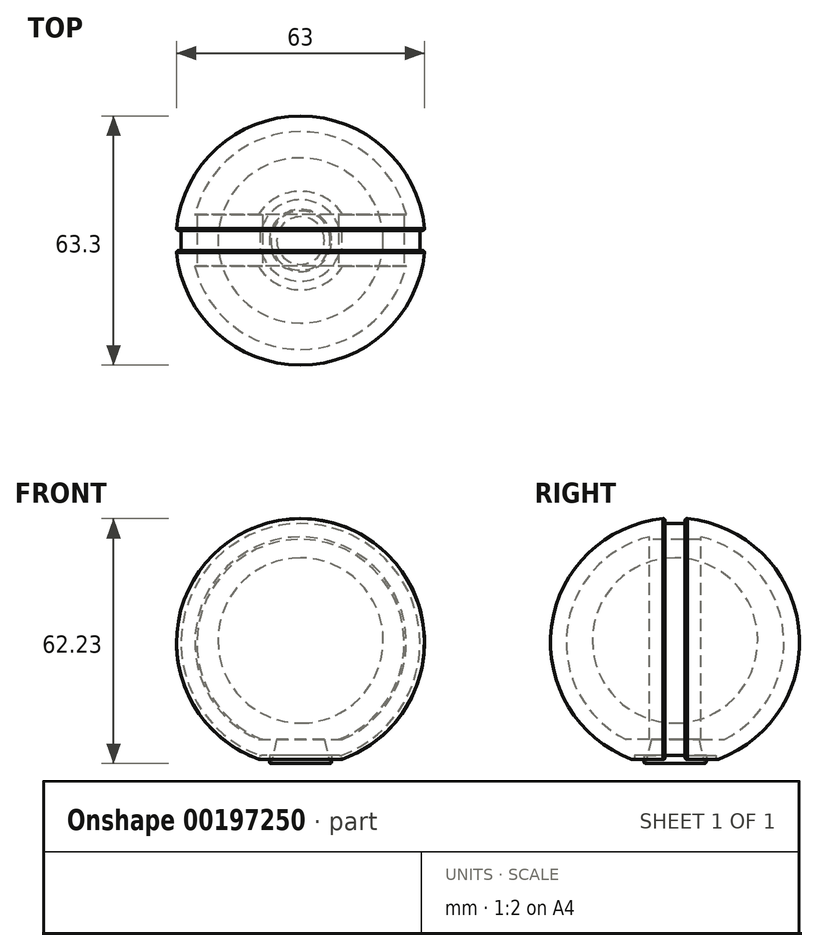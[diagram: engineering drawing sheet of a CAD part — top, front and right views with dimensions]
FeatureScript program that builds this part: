
annotation { "Feature Type Name" : "Feature", "Feature Type Description" : "" }
export const myFeature = defineFeature(function(context is Context, id is Id, definition is map)
    precondition{}
    {
        {
            var Q0;
            Q0=qCreatedBy(makeId("Front.planeOp"),FACE);
            var sketch = newSketch(context, id + "F0", { "sketchPlane" : qUnion([Q0])});
            skLineSegment(sketch, "E0", {"start": v(0, 0) * mm, "end": v(0, 63.3) * mm});
            skArc(sketch, "E1", {"start": v(0, 63.3) * mm, "mid": v(-31.65, 31.65) * mm, "end": v(0, 0) * mm});
            skSolve(sketch);
        }
        {
            var Q0;
            Q0 = qSketchRegion(id + "F0", true);
            var Q1;
            Q1=sQuery(id+"F0.wireOp",EDGE,"E0");
            revolve(context, id + "F1", {"entities" : qUnion([Q0]), "axis" : qUnion([Q1]), "revolveType" : RevolveType.FULL});
        }
        {
            var Q0;
            Q0=qCreatedBy(makeId("Front.planeOp"),FACE);
            var sketch = newSketch(context, id + "F2", { "sketchPlane" : qUnion([Q0])});
            skLineSegment(sketch, "E2", {"start": v(10, -3.8) * mm, "end": v(10, 2.88) * mm});
            skLineSegment(sketch, "E3", {"start": v(-10, 2.88) * mm, "end": v(-10, -3.8) * mm});
            skLineSegment(sketch, "E4", {"start": v(0, 0) * mm, "end": v(0, 63.04) * mm, "construction": true});
            skArc(sketch, "E5", {"start": v(10, 2.88) * mm, "mid": v(0, 61.85) * mm, "end": v(-10, 2.88) * mm});
            skArc(sketch, "E6", {"start": v(10, -3.8) * mm, "mid": v(0, 68.23) * mm, "end": v(-10, -3.8) * mm});
            skSolve(sketch);
        }
        {
            var Q0;
            Q0 = qSketchRegion(id + "F2", true);
            extrude(context, id + "F3", {"entities" : qUnion([Q0]), "operationType" : NewBodyOperationType.REMOVE, "oppositeDirection" : true, "depth" : 2.54 * mm, "hasSecondDirection" : true, "secondDirectionOppositeDirection" : false, "secondDirectionDepth" : 2.54 * mm});
        }
        {
            var Q0;
            Q0 = qSketchRegion(id + "F2", true);
            extrude(context, id + "F4", {"entities" : qUnion([Q0]), "operationType" : NewBodyOperationType.REMOVE, "oppositeDirection" : true, "depth" : 2 * mm, "hasSecondDirection" : true, "secondDirectionOppositeDirection" : false, "secondDirectionDepth" : 2 * mm});
        }
        {
            var Q0;
            Q0=makeQuery(id+"F3.boolean.opBoolean","INTERSECT",EDGE,{"derivedFrom":[makeQuery(id+"F1.opRevolve","SWEPT_FACE",FACE,{"disambiguationData":[OSD([sQuery(id+"F0.wireOp",EDGE,"E1")])]}),makeQuery(id+"F3.opExtrude","CAP_FACE",FACE,{"disambiguationData":[OSD([sQuery(id+"F2.wireOp",EDGE,"E2"),sQuery(id+"F2.wireOp",EDGE,"E3"),sQuery(id+"F2.wireOp",EDGE,"E5"),sQuery(id+"F2.wireOp",EDGE,"E6")])],"isStart":true})]});
            var Q1;
            Q1=makeQuery(id+"F3.boolean.opBoolean","INTERSECT",EDGE,{"derivedFrom":[makeQuery(id+"F1.opRevolve","SWEPT_FACE",FACE,{"disambiguationData":[OSD([sQuery(id+"F0.wireOp",EDGE,"E1")])]}),makeQuery(id+"F3.opExtrude","CAP_FACE",FACE,{"disambiguationData":[OSD([sQuery(id+"F2.wireOp",EDGE,"E2"),sQuery(id+"F2.wireOp",EDGE,"E3"),sQuery(id+"F2.wireOp",EDGE,"E5"),sQuery(id+"F2.wireOp",EDGE,"E6")])],"isStart":false})]});
            fillet(context, id + "F5", {"entities" : qUnion([Q0, Q1]), "radius" : .5 * mm, "tangentPropagation" : true, "allowEdgeOverflow" : false});
        }
        {
            var Q0;
            Q0=makeQuery(id+"F3.boolean.opBoolean","INTERSECT",EDGE,{"derivedFrom":[makeQuery(id+"F1.opRevolve","SWEPT_FACE",FACE,{"disambiguationData":[OSD([sQuery(id+"F0.wireOp",EDGE,"E1")])]}),makeQuery(id+"F3.opExtrude","SWEPT_FACE",FACE,{"disambiguationData":[OSD([sQuery(id+"F2.wireOp",EDGE,"E2")])]})]});
            var Q1;
            Q1=makeQuery(id+"F3.boolean.opBoolean","INTERSECT",EDGE,{"derivedFrom":[makeQuery(id+"F1.opRevolve","SWEPT_FACE",FACE,{"disambiguationData":[OSD([sQuery(id+"F0.wireOp",EDGE,"E1")])]}),makeQuery(id+"F3.opExtrude","SWEPT_FACE",FACE,{"disambiguationData":[OSD([sQuery(id+"F2.wireOp",EDGE,"E3")])]})]});
            fillet(context, id + "F6", {"entities" : qUnion([Q0, Q1]), "radius" : .2 * mm, "tangentPropagation" : true, "allowEdgeOverflow" : false});
        }
        {
            var Q0;
            Q0=qCreatedBy(makeId("Top.planeOp"),FACE);
            var sketch = newSketch(context, id + "F7", { "sketchPlane" : qUnion([Q0])});
            skCircle(sketch, "E7", {"center": v(0, 0) * mm, "radius": 10.36 * mm});
            skCircle(sketch, "E8", {"center": v(0, 0) * mm, "radius": 7.92 * mm});
            skSolve(sketch);
        }
        {
            var Q0;
            Q0 = qSketchRegion(id + "F7", true);
            extrude(context, id + "F8", {"entities" : qUnion([Q0]), "operationType" : NewBodyOperationType.REMOVE, "depth" : 3 * mm});
        }
        {
            var Q0;
            Q0=makeQuery(id+"F8.boolean.opBoolean","INTERSECT",EDGE,{"disambiguationData":[OD(0.0)],"derivedFrom":[makeQuery(id+"F1.opRevolve","SWEPT_FACE",FACE,{"disambiguationData":[OSD([sQuery(id+"F0.wireOp",EDGE,"E1")])]}),makeQuery(id+"F8.opExtrude","SWEPT_FACE",FACE,{"disambiguationData":[OSD([sQuery(id+"F7.wireOp",EDGE,"E7")])]})]});
            var Q1;
            Q1=makeQuery(id+"F8.boolean.opBoolean","INTERSECT",EDGE,{"disambiguationData":[OD(1.0)],"derivedFrom":[makeQuery(id+"F1.opRevolve","SWEPT_FACE",FACE,{"disambiguationData":[OSD([sQuery(id+"F0.wireOp",EDGE,"E1")])]}),makeQuery(id+"F8.opExtrude","SWEPT_FACE",FACE,{"disambiguationData":[OSD([sQuery(id+"F7.wireOp",EDGE,"E7")])]})]});
            fillet(context, id + "F9", {"entities" : qUnion([Q0, Q1]), "radius" : .5 * mm, "tangentPropagation" : true, "allowEdgeOverflow" : false});
        }
        {
            var Q0;
            Q0=qCreatedBy(makeId("Top.planeOp"),FACE);
            var sketch = newSketch(context, id + "F10", { "sketchPlane" : qUnion([Q0])});
            skCircle(sketch, "E9", {"center": v(0, 0) * mm, "radius": 4.15 * mm});
            skSolve(sketch);
        }
        {
            var Q0;
            Q0=makeQuery(id+"F8.boolean.opBoolean","INTERSECT",EDGE,{"derivedFrom":[makeQuery(id+"F1.opRevolve","SWEPT_FACE",FACE,{"disambiguationData":[OSD([sQuery(id+"F0.wireOp",EDGE,"E1")])]}),makeQuery(id+"F8.opExtrude","SWEPT_FACE",FACE,{"disambiguationData":[OSD([sQuery(id+"F7.wireOp",EDGE,"E8")])]})]});
            fillet(context, id + "F11", {"entities" : qUnion([Q0]), "radius" : .5 * mm, "tangentPropagation" : true, "allowEdgeOverflow" : false});
        }
        {
            var Q0;
            Q0=qCreatedBy(makeId("Front.planeOp"),FACE);
            var sketch = newSketch(context, id + "F12", { "sketchPlane" : qUnion([Q0])});
            skLineSegment(sketch, "E10", {"start": v(0, 53.18) * mm, "end": v(0, 11.18) * mm});
            skArc(sketch, "E11", {"start": v(0, 53.18) * mm, "mid": v(-21, 32.18) * mm, "end": v(0, 11.18) * mm});
            skPoint(sketch, "E12.orphan", {"position": v(0, 89.01) * mm});
            skPoint(sketch, "E13.orphan", {"position": v(0, -24.64) * mm});
            skSolve(sketch);
        }
        {
            var Q0;
            Q0 = qSketchRegion(id + "F12", true);
            var Q1;
            Q1=sQuery(id+"F0.wireOp",EDGE,"E0");
            revolve(context, id + "F13", {"entities" : qUnion([Q0]), "axis" : qUnion([Q1]), "revolveType" : RevolveType.FULL});
        }
        {
            var Q0;
            Q0=makeQuery(id+"F8.boolean.opBoolean","SPLIT",FACE,{"disambiguationData":[TD([makeQuery(id+"F8.opExtrude","SWEPT_FACE",FACE,{"disambiguationData":[OSD([sQuery(id+"F7.wireOp",EDGE,"E8")])]})])],"derivedFrom":makeQuery(id+"F1.opRevolve","SWEPT_FACE",FACE,{"disambiguationData":[OSD([sQuery(id+"F0.wireOp",EDGE,"E1")])]})});
            shell(context, id + "F14", {"entities" : qUnion([Q0]), "thickness" : 4 * mm});
        }
    });
